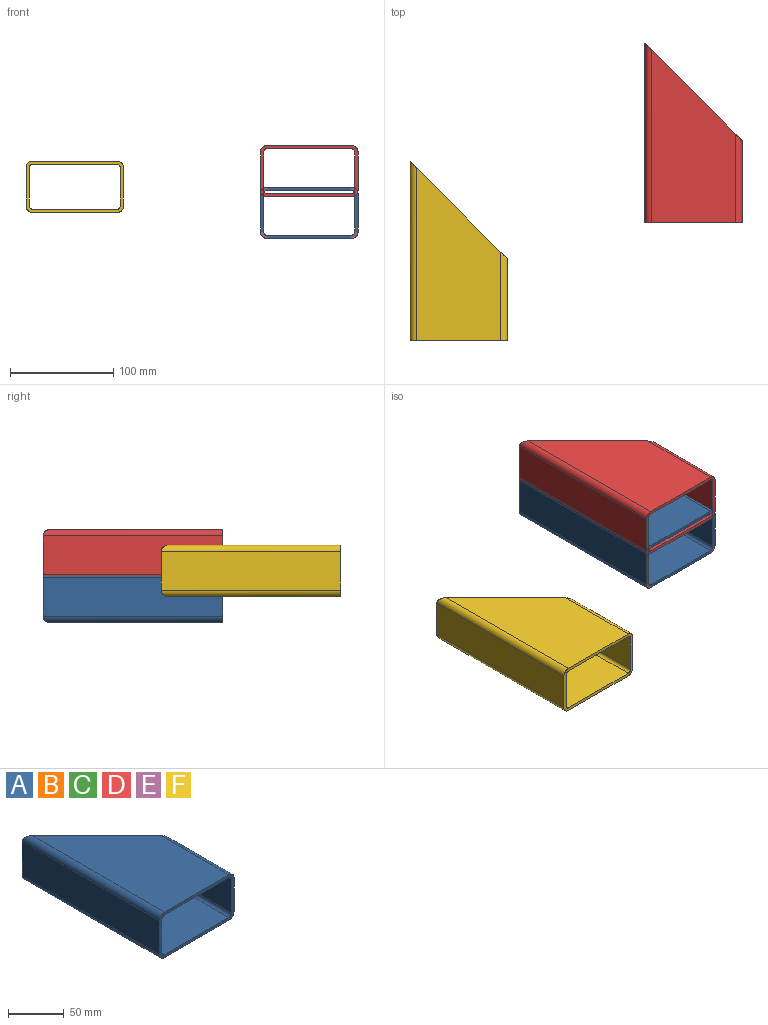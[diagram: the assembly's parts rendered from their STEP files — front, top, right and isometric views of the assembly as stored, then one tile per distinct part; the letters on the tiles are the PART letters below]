
ASSEMBLY  parts=6 mates=1
PART A: 18 faces, bbox 94.6x174.3x50 mm
  f0: plane 79.69x37.28mm, normal (1,0,0), area 2970.5mm2, adj f1,f7,f8,f17
  f1: cylinder r=6.35mm len=86.04mm, axis (0,-1,0), area 817.9mm2, adj f0,f2,f8,f17
  f2: plane 167.96x81.92mm, normal (0,0,-1), area 10403.9mm2, adj f1,f3,f8,f17
  f3: cylinder r=6.35mm len=174.31mm, axis (0,-1,0), area 1715.7mm2, adj f2,f4,f8,f17
  f4: plane 174.31x37.28mm, normal (-1,0,0), area 6497.5mm2, adj f3,f5,f8,f17
  f5: cylinder r=6.35mm len=174.31mm, axis (0,-1,0), area 1715.7mm2, adj f4,f6,f8,f17
  f6: plane 167.96x81.92mm, normal (0,0,1), area 10403.9mm2, adj f5,f7,f8,f17
  f7: cylinder r=6.35mm len=86.04mm, axis (0,-1,0), area 817.9mm2, adj f0,f6,f8,f17
  f8: plane 94.62x49.98mm, normal (0,-1,0), area 851.9mm2, adj f0,f1,f2,f3,f4,f5,f6,f7
  f9: plane 82.86x37.28mm, normal (-1,0,0), area 3088.8mm2, adj f8,f10,f16,f17
  f10: cylinder r=3.17mm len=86.04mm, axis (0,-1,0), area 419mm2, adj f8,f9,f11,f17
  f11: plane 167.96x81.92mm, normal (0,0,-1), area 10403.9mm2, adj f8,f10,f12,f17
  f12: cylinder r=3.17mm len=171.14mm, axis (0,-1,0), area 847.7mm2, adj f8,f11,f13,f17
  f13: plane 171.14x37.28mm, normal (1,0,0), area 6379.2mm2, adj f8,f12,f14,f17
  f14: cylinder r=3.17mm len=171.14mm, axis (0,-1,0), area 847.7mm2, adj f8,f13,f15,f17
  f15: plane 167.96x81.92mm, normal (0,0,1), area 10403.9mm2, adj f8,f14,f16,f17
  f16: cylinder r=3.17mm len=86.04mm, axis (0,-1,0), area 419mm2, adj f8,f9,f15,f17
  f17: plane 94.62x94.62mm, normal (0.71,0.71,0), area 1204.8mm2, adj f0,f1,f2,f3,f4,f5,f6,f7
PART B: same geometry as A
PART C: same geometry as A
PART D: same geometry as A
PART E: same geometry as A
PART F: same geometry as A
PLACE A t=(236.32,156.57,-29.58)mm
PLACE B t=(236.32,156.57,-29.58)mm
PLACE C t=(236.32,156.57,-29.58)mm
PLACE D t=(236.32,156.57,10.87)mm
PLACE E t=(236.32,156.57,-29.58)mm
PLACE F t=(8.68,41.94,-4.38)mm
MATE fastened D.f17 <-> C.f17  axis (0.71,0.71,0) through (195.36,197.53,-7.77)mm
